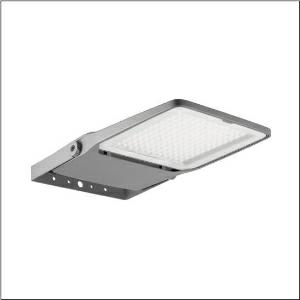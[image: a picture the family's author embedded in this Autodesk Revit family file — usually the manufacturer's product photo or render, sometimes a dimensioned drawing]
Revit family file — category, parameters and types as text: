
# Revit family: floodlight_fl_20_midi___pl43_5xa7682e1a2ac_d3d8
name_source: partatom
category: Lighting Fixtures
units: mm (PartAtom-declared; Revit-internal decimal feet)

## family parameters
Cut with Voids When Loaded = No
Host = Face
Light Source = No
Part Type = Normal
Room Calculation Point = No
Round Connector Dimension = Use Diameter
Shared = No

## types (1)
- --- (1 x LED 3000K / CRI = 80 (unbekannt), 22300 lm, 3000K)
    Apparent Load = 208 VA
    CIE Flux Codes = 32 74 99 100 100
    Color Rendering = 80
    Color Temperature = 3000K
    Default Elevation = 1800 mm
    Description = Floodlight FL 20 midi, floodlight, primary light control with lens, of plastic, primary optical cover: protective disc, of toughened safety glass, transparent, light distribution: PL43, light emission: direct distribution, primary light characteristic: asymmetric, installation type: surface-mounted, LED High Power LED, rated luminous flux: 22.300 lm, light colour: 830, colour temperature: 3000K, control gear: ECG Plus, control: flexible luminous flux parameterisation, time-dependent luminous flux control, digital communication interface, power reduction, overheat protection, electronic power reduction, with terminal, 5-pole, max. 2.5mm², mains connection: 220..240V, AC, 50/60Hz, rated input power: 208W, LED unit, of diecast aluminium, powder-coated, Siteco® metallic grey (DB 702S), length: 731 mm, width: 450 mm, height: 76mm, housing frame, of diecast aluminium, powder-coated, Siteco® metallic grey (DB 702S), wall fastening, of steel, powder-coated, Siteco® metallic grey (DB 702S), DALIprotection rating (complete): IP66, insulation class (complete): insulation class II (safety insulation), certification: CE, ENEC, VDE, protection symbol: D, permissible ambient temperature for indoor applications: -40..+40°C, permissible ambient temperature for outdoor applications: -40..+50°C, standard: DIN EN 12944, packaging unit: 1 piece

Light Distribution: PL43
    Height = 76 mm
    Lamp = 1 x LED 3000K / CRI >= 80 (unbekannt)
    Lamp Light Flux = 22300 lm
    Lamp count = 1
    Length = 731 mm
    Luminous efficacy = 107 lm/W
    Manufacturer = Siteco
    ModVariant = No
    Model = 5XA7682E1A2AC
    Number of Poles = 1
    OnlyDefault = Yes
    Power Factor = 1
    Product Name = Floodlight FL 20 midi | PL43
    Product group = floodlight | pylon top
    ProductGroupID = 6101
    Protection Class = Protection class II
    Protection Degree = IP 66
    RLX_Detail_Level = 1
    RlxData = <blob elided: 91793 chars, md5=69d1dc71>
    Socket = socket
    Standby Power = 0 W
    System Light Flux = 22300 lm
    System Power = 208 W
    Type Comments = factory setting: luminous flux: 100 % | dim-lin: 254 | 484 mA
    Type Image = l_1005944.jpg
    URL = http://relux.com
    VarID = @adj_143767
    Voltage = 0 V
    Weight = 0.00 kg
    Width = 450 mm

## geometry (parser evidence)
native form markers: Blend x4, Sweep x13
no freeform markers — native parametric forms only
